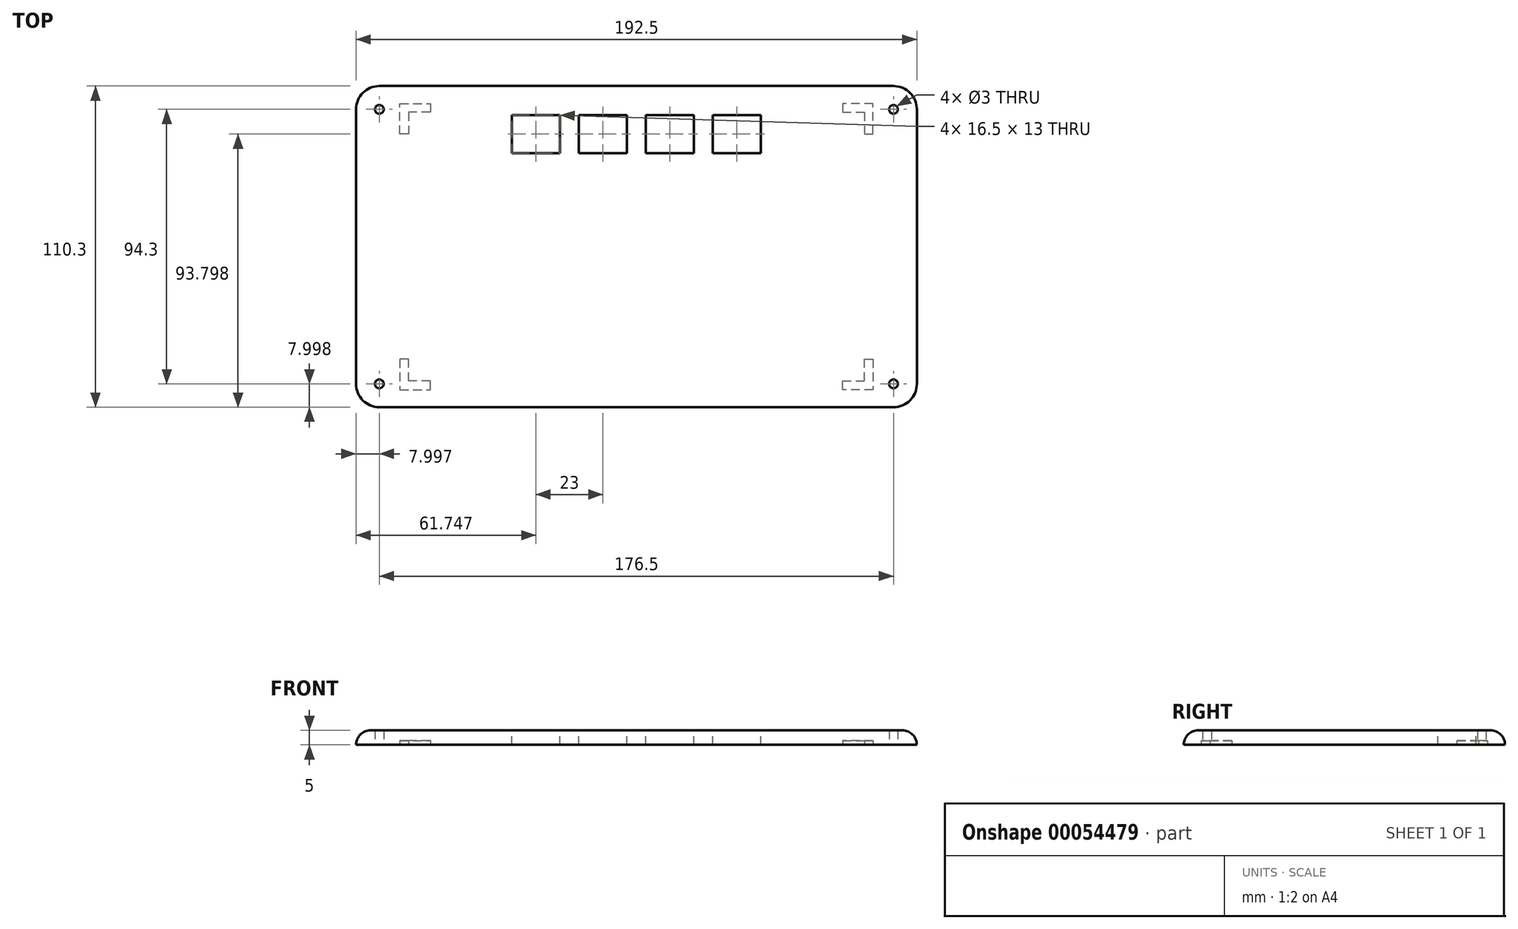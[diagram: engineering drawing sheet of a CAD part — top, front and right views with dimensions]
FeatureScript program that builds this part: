
annotation { "Feature Type Name" : "Feature", "Feature Type Description" : "" }
export const myFeature = defineFeature(function(context is Context, id is Id, definition is map)
    precondition{}
    {
        {
            var Q0;
            Q0=qCreatedBy(makeId("Top.planeOp"),FACE);
            var sketch = newSketch(context, id + "F0", { "sketchPlane" : qUnion([Q0])});
            skLineSegment(sketch, "E0.bottom", {"start": v(-53.67, -23.88) * mm, "end": v(122.83, -23.88) * mm});
            skLineSegment(sketch, "E0.top", {"start": v(-53.67, 86.42) * mm, "end": v(122.83, 86.42) * mm});
            skLineSegment(sketch, "E0.left", {"start": v(-61.67, -15.88) * mm, "end": v(-61.67, 78.42) * mm});
            skLineSegment(sketch, "E0.right", {"start": v(130.83, -15.88) * mm, "end": v(130.83, 78.42) * mm});
            skPoint(sketch, "E1.visualSharp", {"position": v(-61.67, -23.88) * mm});
            skArc(sketch, "E1.filletArc", {"start": v(-61.67, -15.88) * mm, "mid": v(-59.33, -21.54) * mm, "end": v(-53.67, -23.88) * mm});
            skPoint(sketch, "E2.visualSharp", {"position": v(130.83, -23.88) * mm});
            skArc(sketch, "E2.filletArc", {"start": v(122.83, -23.88) * mm, "mid": v(128.48, -21.54) * mm, "end": v(130.83, -15.88) * mm});
            skPoint(sketch, "E3.visualSharp", {"position": v(130.83, 86.42) * mm});
            skArc(sketch, "E3.filletArc", {"start": v(130.83, 78.42) * mm, "mid": v(128.48, 84.07) * mm, "end": v(122.83, 86.42) * mm});
            skPoint(sketch, "E4.visualSharp", {"position": v(-61.67, 86.42) * mm});
            skArc(sketch, "E4.filletArc", {"start": v(-53.67, 86.42) * mm, "mid": v(-59.33, 84.07) * mm, "end": v(-61.67, 78.42) * mm});
            skSolve(sketch);
        }
        {
            var Q0;
            Q0=makeQuery(id+"F0.imprint","IMPRINT",FACE,{"disambiguationData":[TD([[makeQuery(id+"F0.imprint","IMPRINT",EDGE,{"derivedFrom":sQuery(id+"F0.wireOp",EDGE,"E0.bottom")}),1.0]])]});
            extrude(context, id + "F1", {"entities" : qUnion([Q0]), "oppositeDirection" : true, "depth" : 5 * mm});
        }
        {
            var Q0;
            Q0=makeQuery(id+"F1.opExtrude","CAP_FACE",FACE,{"disambiguationData":[OSD([sQuery(id+"F0.wireOp",EDGE,"E0.bottom"),sQuery(id+"F0.wireOp",EDGE,"E0.top"),sQuery(id+"F0.wireOp",EDGE,"E0.left"),sQuery(id+"F0.wireOp",EDGE,"E0.right"),sQuery(id+"F0.wireOp",EDGE,"E1.filletArc"),sQuery(id+"F0.wireOp",EDGE,"E2.filletArc"),sQuery(id+"F0.wireOp",EDGE,"E3.filletArc"),sQuery(id+"F0.wireOp",EDGE,"E4.filletArc")])],"isStart":false});
            var sketch = newSketch(context, id + "F2", { "sketchPlane" : qUnion([Q0])});
            skCircle(sketch, "E5", {"center": v(-53.67, 15.88) * mm, "radius": 1.5 * mm});
            skLineSegment(sketch, "E6", {"start": v(34.58, 23.88) * mm, "end": v(34.58, -86.42) * mm, "construction": true});
            skLineSegment(sketch, "E7", {"start": v(-61.67, -31.27) * mm, "end": v(130.83, -31.27) * mm, "construction": true});
            skCircle(sketch, "E8.MirrorC", {"center": v(122.83, 15.88) * mm, "radius": 1.5 * mm});
            skCircle(sketch, "E9.MirrorC", {"center": v(122.83, -78.42) * mm, "radius": 1.5 * mm});
            skCircle(sketch, "E10.MirrorC", {"center": v(-53.67, -78.42) * mm, "radius": 1.5 * mm});
            skSolve(sketch);
        }
        {
            var Q0;
            Q0 = qSketchRegion(id + "F2", true);
            extrude(context, id + "F3", {"entities" : qUnion([Q0]), "operationType" : NewBodyOperationType.REMOVE, "endBound" : BoundingType.THROUGH_ALL, "oppositeDirection" : true, "depth" : 25 * mm});
        }
        {
            var Q0;
            Q0=makeQuery(id+"F1.opExtrude","CAP_FACE",FACE,{"disambiguationData":[OSD([sQuery(id+"F0.wireOp",EDGE,"E0.bottom"),sQuery(id+"F0.wireOp",EDGE,"E0.top"),sQuery(id+"F0.wireOp",EDGE,"E0.left"),sQuery(id+"F0.wireOp",EDGE,"E0.right"),sQuery(id+"F0.wireOp",EDGE,"E1.filletArc"),sQuery(id+"F0.wireOp",EDGE,"E2.filletArc"),sQuery(id+"F0.wireOp",EDGE,"E3.filletArc"),sQuery(id+"F0.wireOp",EDGE,"E4.filletArc")])],"isStart":false});
            extrude(context, id + "F4", {"entities" : qUnion([Q0]), "operationType" : NewBodyOperationType.REMOVE, "depth" : 25 * mm});
        }
        {
            var Q0;
            Q0=makeQuery(id+"F1.opExtrude","CAP_EDGE",EDGE,{"disambiguationData":[OSD([sQuery(id+"F0.wireOp",EDGE,"E0.top")])],"isStart":true});
            var Q1;
            Q1=makeQuery(id+"F1.opExtrude","CAP_EDGE",EDGE,{"disambiguationData":[OSD([sQuery(id+"F0.wireOp",EDGE,"E3.filletArc")])],"isStart":true});
            var Q2;
            Q2=makeQuery(id+"F1.opExtrude","CAP_EDGE",EDGE,{"disambiguationData":[OSD([sQuery(id+"F0.wireOp",EDGE,"E0.right")])],"isStart":true});
            var Q3;
            Q3=makeQuery(id+"F1.opExtrude","CAP_EDGE",EDGE,{"disambiguationData":[OSD([sQuery(id+"F0.wireOp",EDGE,"E2.filletArc")])],"isStart":true});
            var Q4;
            Q4=makeQuery(id+"F1.opExtrude","CAP_EDGE",EDGE,{"disambiguationData":[OSD([sQuery(id+"F0.wireOp",EDGE,"E0.bottom")])],"isStart":true});
            var Q5;
            Q5=makeQuery(id+"F1.opExtrude","CAP_EDGE",EDGE,{"disambiguationData":[OSD([sQuery(id+"F0.wireOp",EDGE,"E1.filletArc")])],"isStart":true});
            var Q6;
            Q6=makeQuery(id+"F1.opExtrude","CAP_EDGE",EDGE,{"disambiguationData":[OSD([sQuery(id+"F0.wireOp",EDGE,"E0.left")])],"isStart":true});
            var Q7;
            Q7=makeQuery(id+"F1.opExtrude","CAP_EDGE",EDGE,{"disambiguationData":[OSD([sQuery(id+"F0.wireOp",EDGE,"E4.filletArc")])],"isStart":true});
            fillet(context, id + "F5", {"entities" : qUnion([Q0, Q1, Q2, Q3, Q4, Q5, Q6, Q7]), "radius" : 5 * mm, "tangentPropagation" : true, "allowEdgeOverflow" : false});
        }
        {
            var Q0;
            Q0=makeQuery(id+"F1.opExtrude","CAP_FACE",FACE,{"disambiguationData":[OSD([sQuery(id+"F0.wireOp",EDGE,"E0.bottom"),sQuery(id+"F0.wireOp",EDGE,"E0.top"),sQuery(id+"F0.wireOp",EDGE,"E0.left"),sQuery(id+"F0.wireOp",EDGE,"E0.right"),sQuery(id+"F0.wireOp",EDGE,"E1.filletArc"),sQuery(id+"F0.wireOp",EDGE,"E2.filletArc"),sQuery(id+"F0.wireOp",EDGE,"E3.filletArc"),sQuery(id+"F0.wireOp",EDGE,"E4.filletArc")])],"isStart":true});
            var sketch = newSketch(context, id + "F6", { "sketchPlane" : qUnion([Q0])});
            skLineSegment(sketch, "E11.bottom", {"start": v(-8.17, 76.42) * mm, "end": v(8.33, 76.42) * mm});
            skLineSegment(sketch, "E11.top", {"start": v(-8.17, 63.42) * mm, "end": v(8.33, 63.42) * mm});
            skLineSegment(sketch, "E11.left", {"start": v(-8.17, 76.42) * mm, "end": v(-8.17, 63.42) * mm});
            skLineSegment(sketch, "E11.right", {"start": v(8.33, 76.42) * mm, "end": v(8.33, 63.42) * mm});
            skLineSegment(sketch, "E12.1.0.0", {"start": v(31.33, 76.42) * mm, "end": v(31.33, 63.42) * mm});
            skLineSegment(sketch, "E12.1.0.1", {"start": v(14.83, 76.42) * mm, "end": v(14.83, 63.42) * mm});
            skLineSegment(sketch, "E12.1.0.2", {"start": v(14.83, 76.42) * mm, "end": v(31.33, 76.42) * mm});
            skLineSegment(sketch, "E12.1.0.3", {"start": v(14.83, 63.42) * mm, "end": v(31.33, 63.42) * mm});
            skLineSegment(sketch, "E12.2.0.0", {"start": v(54.33, 76.42) * mm, "end": v(54.33, 63.42) * mm});
            skLineSegment(sketch, "E12.2.0.1", {"start": v(37.83, 76.42) * mm, "end": v(37.83, 63.42) * mm});
            skLineSegment(sketch, "E12.2.0.2", {"start": v(37.83, 76.42) * mm, "end": v(54.33, 76.42) * mm});
            skLineSegment(sketch, "E12.2.0.3", {"start": v(37.83, 63.42) * mm, "end": v(54.33, 63.42) * mm});
            skLineSegment(sketch, "E12.3.0.0", {"start": v(77.33, 76.42) * mm, "end": v(77.33, 63.42) * mm});
            skLineSegment(sketch, "E12.3.0.1", {"start": v(60.83, 76.42) * mm, "end": v(60.83, 63.42) * mm});
            skLineSegment(sketch, "E12.3.0.2", {"start": v(60.83, 76.42) * mm, "end": v(77.33, 76.42) * mm});
            skLineSegment(sketch, "E12.3.0.3", {"start": v(60.83, 63.42) * mm, "end": v(77.33, 63.42) * mm});
            skLineSegment(sketch, "E12.direction1", {"start": v(8.33, 63.42) * mm, "end": v(31.33, 63.42) * mm, "construction": true});
            skLineSegment(sketch, "E13", {"start": v(34.58, -23.88) * mm, "end": v(34.58, 86.42) * mm, "construction": true});
            skSolve(sketch);
        }
        {
            var Q0;
            Q0 = qSketchRegion(id + "F6", true);
            extrude(context, id + "F7", {"entities" : qUnion([Q0]), "operationType" : NewBodyOperationType.REMOVE, "endBound" : BoundingType.THROUGH_ALL, "oppositeDirection" : true, "depth" : 25 * mm});
        }
        {
            var Q0;
            Q0=makeQuery(id+"F1.opExtrude","CAP_FACE",FACE,{"disambiguationData":[OSD([sQuery(id+"F0.wireOp",EDGE,"E0.bottom"),sQuery(id+"F0.wireOp",EDGE,"E0.top"),sQuery(id+"F0.wireOp",EDGE,"E0.left"),sQuery(id+"F0.wireOp",EDGE,"E0.right"),sQuery(id+"F0.wireOp",EDGE,"E1.filletArc"),sQuery(id+"F0.wireOp",EDGE,"E2.filletArc"),sQuery(id+"F0.wireOp",EDGE,"E3.filletArc"),sQuery(id+"F0.wireOp",EDGE,"E4.filletArc")])],"isStart":false});
            var sketch = newSketch(context, id + "F8", { "sketchPlane" : qUnion([Q0])});
            skLineSegment(sketch, "E14", {"start": v(-61.67, -31.27) * mm, "end": v(130.83, -31.27) * mm, "construction": true});
            skLineSegment(sketch, "E15", {"start": v(-46.67, -69.92) * mm, "end": v(-46.67, -80.42) * mm});
            skLineSegment(sketch, "E16", {"start": v(-46.67, -80.42) * mm, "end": v(-36.17, -80.42) * mm});
            skLineSegment(sketch, "E17", {"start": v(-36.17, -80.42) * mm, "end": v(-36.17, -77.42) * mm});
            skLineSegment(sketch, "E18", {"start": v(-36.17, -77.42) * mm, "end": v(-43.67, -77.42) * mm});
            skLineSegment(sketch, "E19", {"start": v(-43.67, -77.42) * mm, "end": v(-43.67, -69.92) * mm});
            skLineSegment(sketch, "E20", {"start": v(-43.67, -69.92) * mm, "end": v(-46.67, -69.92) * mm});
            skLineSegment(sketch, "E21.MirrorCS", {"start": v(-43.67, 7.38) * mm, "end": v(-46.67, 7.38) * mm});
            skLineSegment(sketch, "E22.MirrorCS", {"start": v(-36.17, 17.88) * mm, "end": v(-36.17, 14.88) * mm});
            skLineSegment(sketch, "E23.MirrorCS", {"start": v(-43.67, 14.88) * mm, "end": v(-43.67, 7.38) * mm});
            skLineSegment(sketch, "E24.MirrorCS", {"start": v(-36.17, 14.88) * mm, "end": v(-43.67, 14.88) * mm});
            skLineSegment(sketch, "E25.MirrorCS", {"start": v(-46.67, 17.88) * mm, "end": v(-36.17, 17.88) * mm});
            skLineSegment(sketch, "E26.MirrorCS", {"start": v(-46.67, 7.38) * mm, "end": v(-46.67, 17.88) * mm});
            skLineSegment(sketch, "E27.MirrorCS", {"start": v(105.33, 17.88) * mm, "end": v(105.33, 14.88) * mm});
            skLineSegment(sketch, "E28.MirrorCS", {"start": v(112.83, 7.38) * mm, "end": v(115.83, 7.38) * mm});
            skLineSegment(sketch, "E29.MirrorCS", {"start": v(112.83, -69.92) * mm, "end": v(115.83, -69.92) * mm});
            skLineSegment(sketch, "E30.MirrorCS", {"start": v(105.33, -80.42) * mm, "end": v(105.33, -77.42) * mm});
            skLineSegment(sketch, "E31.MirrorCS", {"start": v(115.83, 7.38) * mm, "end": v(115.83, 17.88) * mm});
            skLineSegment(sketch, "E32.MirrorCS", {"start": v(115.83, 17.88) * mm, "end": v(105.33, 17.88) * mm});
            skLineSegment(sketch, "E33.MirrorCS", {"start": v(105.33, 14.88) * mm, "end": v(112.83, 14.88) * mm});
            skLineSegment(sketch, "E34.MirrorCS", {"start": v(112.83, 14.88) * mm, "end": v(112.83, 7.38) * mm});
            skLineSegment(sketch, "E35.MirrorCS", {"start": v(112.83, -77.42) * mm, "end": v(112.83, -69.92) * mm});
            skLineSegment(sketch, "E36.MirrorCS", {"start": v(105.33, -77.42) * mm, "end": v(112.83, -77.42) * mm});
            skLineSegment(sketch, "E37.MirrorCS", {"start": v(115.83, -69.92) * mm, "end": v(115.83, -80.42) * mm});
            skLineSegment(sketch, "E38.MirrorCS", {"start": v(115.83, -80.42) * mm, "end": v(105.33, -80.42) * mm});
            skSolve(sketch);
        }
        {
            var Q0;
            Q0 = qSketchRegion(id + "F8", true);
            extrude(context, id + "F9", {"entities" : qUnion([Q0]), "operationType" : NewBodyOperationType.REMOVE, "oppositeDirection" : true, "depth" : 1.5 * mm});
        }
    });
